# Revit family: ledwaterproof-e3_l1500-44_55w-865_531000012400_db47
name_source: partatom
category: Lighting Fixtures
units: mm (PartAtom-declared; Revit-internal decimal feet)

## family parameters
Cut with Voids When Loaded = No
Host = Face
Light Source = No
Part Type = Normal
Room Calculation Point = No
Round Connector Dimension = Use Diameter
Shared = No

## types (1)
- LEDWaterproof-E3 L1500-44/55W-865 (1 x LED, 8250 lm, 6500)
    Apparent Load = 55 VA
    Approval mark = CE
    CIE Flux Codes = 41 71 90 89 120
    Color Rendering = 80
    Color Temperature = 6500
    Control Gear = Electronic ballast
    Default Elevation = 1800 mm
    Description = Waterproof luminaire in "sealed-for-life" concept. Improved installation due to new twist-and-lock endcap. Supplied with vandal-proof stainless steel ceiling and suspension clips. Equipped with 3x2.5mm² throughwiring.
    Frequency = 60 Hz
    Height = 60 mm  [stored 0.19685 ft]
    Lamp = 1 x LED
    Lamp Light Flux = 8250 lm
    Lamp count = 1
    Length = 1556 mm
    Luminous efficacy = 179 lm/W
    Manufacturer = OPPLE
    ModVariant = No
    Model = 531000012400
    Number of Poles = 1
    OnlyDefault = Yes
    Power Factor = 1
    Product Name = LEDWaterproof-E3 L1500-44/55W-865
    Product group = Ceiling / wall-mounted luminaires
    ProductGroupID = 30
    Protection Class = Protection class II
    Protection Degree = IP 65
    RLX_Detail_Level = 1
    RlxData = <blob elided: 139369 chars, md5=d1c0d622>
    Socket = socket
    Standby Power = 0 W
    System Light Flux = 9862 lm
    System Power = 55 W
    Type Comments = Product without accessories
    Type Image = web_wp_e3.jpg
    URL = http://relux.com
    VarID = ---
    Voltage = 230 V
    Voltage Range = 220-240 V
    Weight = 0.00 kg
    Width = 62 mm  [stored 0.203412 ft]

note: [stored X ft] marks values corroborated as IEEE doubles in the binary element streams (Revit-internal decimal feet)

## geometry (parser evidence)
native form markers: Blend x4, Sweep x11
no freeform markers — native parametric forms only
